# Revit family: IS_TonicII_A6327_BIM_DE
name_source: partatom
category: Plumbing Fixtures
revit_build: Autodesk Revit MEP 2016 (Build: 20161004_0715(x64)
units: mm (PartAtom-declared; Revit-internal decimal feet)

## family parameters
Cut with Voids When Loaded = No
Host = Face
OmniClass Number = 23.45.55.17
OmniClass Title = Mixing Faucets
Part Type = Normal
Room Calculation Point = No
Round Connector Dimension = Use Diameter
Shared = Yes

## types (1)
- A6327AA - TONIC II BSN MXR RMTD CHR 5L/MIN
    Accessories = www.idealstandard.de\ersatzteile
    AreaUnits = millimeters
    Assembly Code = C1030200
    AssetType = Fixed
    BIMObjectName = ISI_IdealStandard_MixerTaps_TONIC II_A6327AA
    BarCode = 4015413334945
    Brand = Ideal Standard
    CWFU = 0
    CodePerformance = 0
    Color = Chrome
    ConnectionType = Plumbing
    Cost = 0 $
    CurrencyUnit = €
    Default Elevation = 800 mm  [stored 2.62467 ft]
    Description = TONIC II BSN MXR RMTD CHR 5L/MIN
    DurationUnit = year
    ExpectedLife = 25
    Features = TONIC II single lever one hole basin mixer, no pop-up waste
    Finish = Chrome
    GrossWeight = 1,85 kg
    HWFU = 0
    InstallationDate = 1900-12-31T23:59:59
    InstallationInstructions = www.idealstandard.de\produkte
    LinearUnits = millimeters
    ManufacturerURL = www.idealstandard.de
    Material = Brass
    Model = A6327AA
    ModelNumber = A6327AA
    ModelReference = IS Waschtischarmatur TONIC II, 5 l/min., o.Ablgarn., Ausld. 126mm, Chrom
    Name = ISI_IdealStandard_MixerTaps_TONIC II_A6327AA
    NominalDepth = 0 mm  [stored 0 ft]
    NominalHeight = 155 mm
    NominalLength = 172 mm
    NominalWidth = 51 mm
    ProductInformation = www.idealstandard.de
    Shape = Sculptured
    Size = 171 x 51 x 154 mm
    Space = Internal
    URL = www.idealstandard.de
    Uniclass2015Code = Pr_40_20_87_98
    Uniclass2015Title = Washbasin taps
    Uniclass2015Version = Products v1.1
    Version = 1
    VolumeUnits = Litres
    WFU = 0

note: [stored X ft] marks values corroborated as IEEE doubles in the binary element streams (Revit-internal decimal feet)

## geometry (parser evidence)
native form markers: Blend x4, Sweep x1
no freeform markers — native parametric forms only
